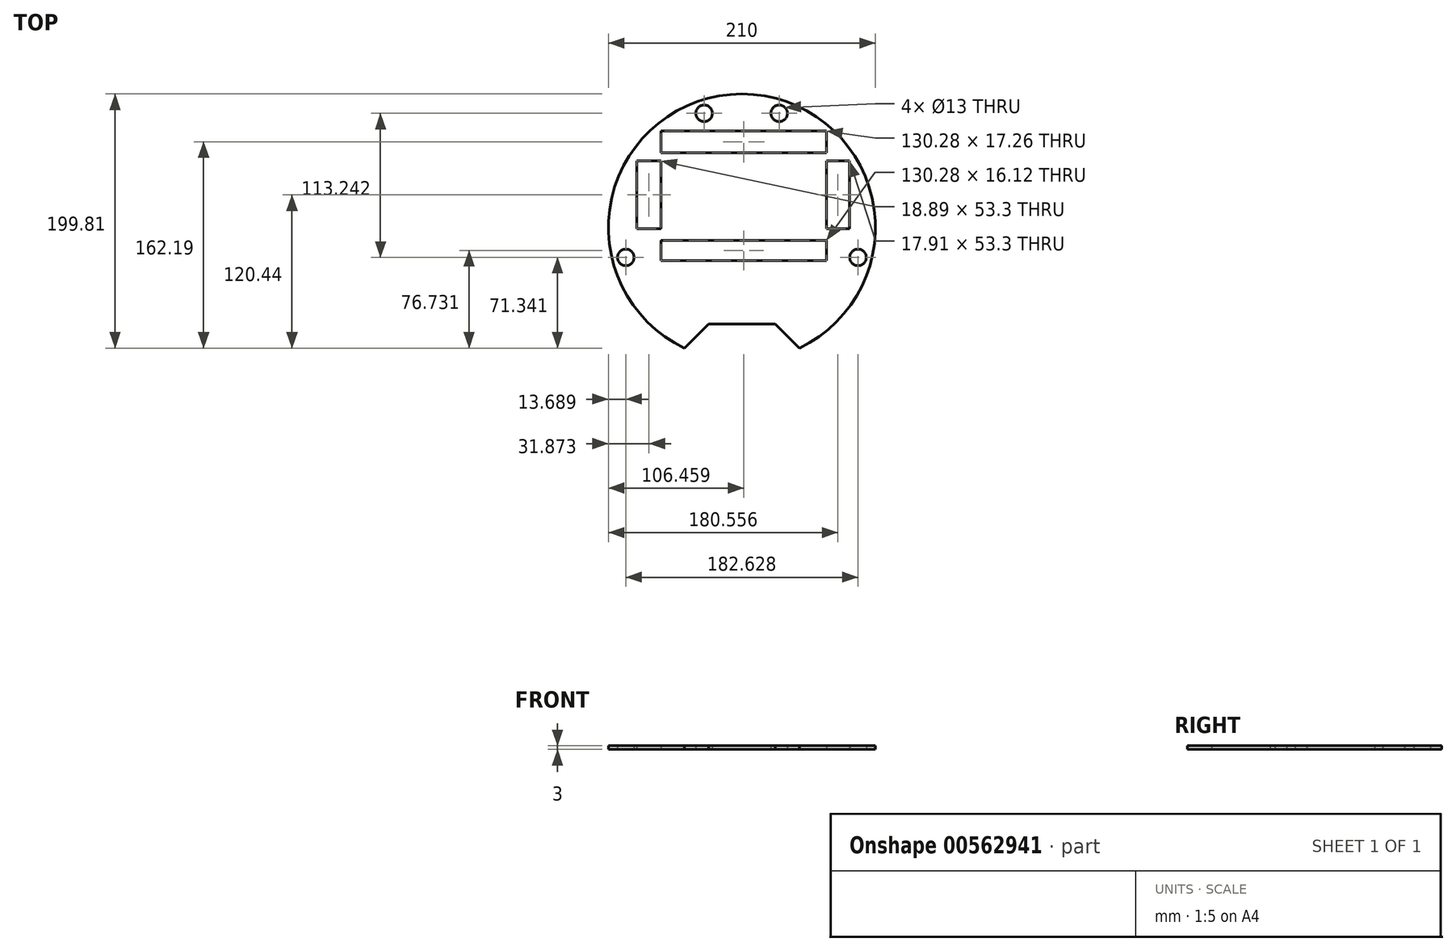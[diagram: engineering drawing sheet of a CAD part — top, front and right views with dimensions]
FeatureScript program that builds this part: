
annotation { "Feature Type Name" : "Feature", "Feature Type Description" : "" }
export const myFeature = defineFeature(function(context is Context, id is Id, definition is map)
    precondition{}
    {
        {
            var Q0;
            Q0=qCreatedBy(makeId("Top.planeOp"),FACE);
            var sketch = newSketch(context, id + "F0", { "sketchPlane" : qUnion([Q0])});
            skCircle(sketch, "E0", {"center": v(-0.03, 1.02) * mm, "radius": 105 * mm});
            skLineSegment(sketch, "E1", {"start": v(-0.03, 106.02) * mm, "end": v(-0.03, -103.98) * mm});
            skLineSegment(sketch, "E2", {"start": v(-0.03, 1.02) * mm, "end": v(-0.03, 106.02) * mm});
            skCircle(sketch, "E3", {"center": v(-29.75, 90.8) * mm, "radius": 6.5 * mm});
            skCircle(sketch, "E4", {"center": v(29.27, 90.8) * mm, "radius": 6.5 * mm});
            skCircle(sketch, "E5", {"center": v(-91.34, -22.45) * mm, "radius": 6.5 * mm});
            skCircle(sketch, "E6", {"center": v(91.29, -22.45) * mm, "radius": 6.5 * mm});
            skLineSegment(sketch, "E7", {"start": v(-0.03, -48.65) * mm, "end": v(-0.03, -63.7) * mm});
            skLineSegment(sketch, "E8", {"start": v(-26.15, -74.78) * mm, "end": v(26.1, -74.78) * mm});
            skLineSegment(sketch, "E9", {"start": v(-26.15, -74.78) * mm, "end": v(-45.16, -93.79) * mm});
            skLineSegment(sketch, "E10", {"start": v(26.1, -74.78) * mm, "end": v(45.1, -93.79) * mm});
            skLineSegment(sketch, "E11.bottom", {"start": v(-50.83, 53.3) * mm, "end": v(50.77, 53.3) * mm});
            skLineSegment(sketch, "E11.top", {"start": v(-50.83, 0) * mm, "end": v(50.77, 0) * mm});
            skLineSegment(sketch, "E11.left", {"start": v(-50.83, 53.3) * mm, "end": v(-50.83, 0) * mm});
            skLineSegment(sketch, "E11.right", {"start": v(50.77, 53.3) * mm, "end": v(50.77, 0) * mm});
            skLineSegment(sketch, "E12.bottom", {"start": v(-63.71, 77.03) * mm, "end": v(66.57, 77.03) * mm});
            skLineSegment(sketch, "E12.top", {"start": v(-63.71, 59.77) * mm, "end": v(66.57, 59.77) * mm});
            skLineSegment(sketch, "E12.left", {"start": v(-63.71, 77.03) * mm, "end": v(-63.71, 59.77) * mm});
            skLineSegment(sketch, "E12.right", {"start": v(66.57, 77.03) * mm, "end": v(66.57, 59.77) * mm});
            skPoint(sketch, "E13.firstSnap0", {"position": v(-0.03, 53.3) * mm});
            skLineSegment(sketch, "E13.bottom", {"start": v(66.57, 53.3) * mm, "end": v(84.48, 53.3) * mm});
            skLineSegment(sketch, "E13.top", {"start": v(66.57, 0) * mm, "end": v(84.48, 0) * mm});
            skLineSegment(sketch, "E13.left", {"start": v(66.57, 53.3) * mm, "end": v(66.57, 0) * mm});
            skLineSegment(sketch, "E13.right", {"start": v(84.48, 53.3) * mm, "end": v(84.48, 0) * mm});
            skLineSegment(sketch, "E14.bottom", {"start": v(-63.71, 53.3) * mm, "end": v(-82.6, 53.3) * mm});
            skLineSegment(sketch, "E14.top", {"start": v(-63.71, 0) * mm, "end": v(-82.6, 0) * mm});
            skLineSegment(sketch, "E14.left", {"start": v(-63.71, 53.3) * mm, "end": v(-63.71, 0) * mm});
            skLineSegment(sketch, "E14.right", {"start": v(-82.6, 53.3) * mm, "end": v(-82.6, 0) * mm});
            skLineSegment(sketch, "E15.bottom", {"start": v(-63.71, -9) * mm, "end": v(66.57, -9) * mm});
            skLineSegment(sketch, "E15.top", {"start": v(-63.71, -25.12) * mm, "end": v(66.57, -25.12) * mm});
            skLineSegment(sketch, "E15.left", {"start": v(-63.71, -9) * mm, "end": v(-63.71, -25.12) * mm});
            skLineSegment(sketch, "E15.right", {"start": v(66.57, -9) * mm, "end": v(66.57, -25.12) * mm});
            skSolve(sketch);
        }
        {
            var Q0;
            Q0=makeQuery(id+"F0.imprint","IMPRINT",FACE,{"disambiguationData":[TD([[makeQuery(id+"F0.imprint","IMPRINT",EDGE,{"derivedFrom":sQuery(id+"F0.wireOp",EDGE,"E3")}),-1.0]])]});
            var Q1;
            Q1=makeQuery(id+"F0.imprint","IMPRINT",FACE,{"disambiguationData":[TD([[makeQuery(id+"F0.imprint","IMPRINT",EDGE,{"derivedFrom":sQuery(id+"F0.wireOp",EDGE,"E4")}),-1.0]])]});
            var Q2;
            {var subQ3=sQuery(id+"F0.wireOp",EDGE,"E11.right");Q2=makeQuery(id+"F0.imprint","IMPRINT",FACE,{"disambiguationData":[TD([[makeQuery(id+"F0.imprint","IMPRINT",EDGE,{"derivedFrom":subQ3}),-1.0]])]});}
            var Q3;
            {var subQ3=sQuery(id+"F0.wireOp",EDGE,"E11.left");Q3=makeQuery(id+"F0.imprint","IMPRINT",FACE,{"disambiguationData":[TD([[makeQuery(id+"F0.imprint","IMPRINT",EDGE,{"derivedFrom":subQ3}),1.0]])]});}
            extrude(context, id + "F1", {"entities" : qUnion([Q0, Q1, Q2, Q3]), "depth" : 3 * mm, "offsetDistance" : 25.4 * mm});
        }
    });
